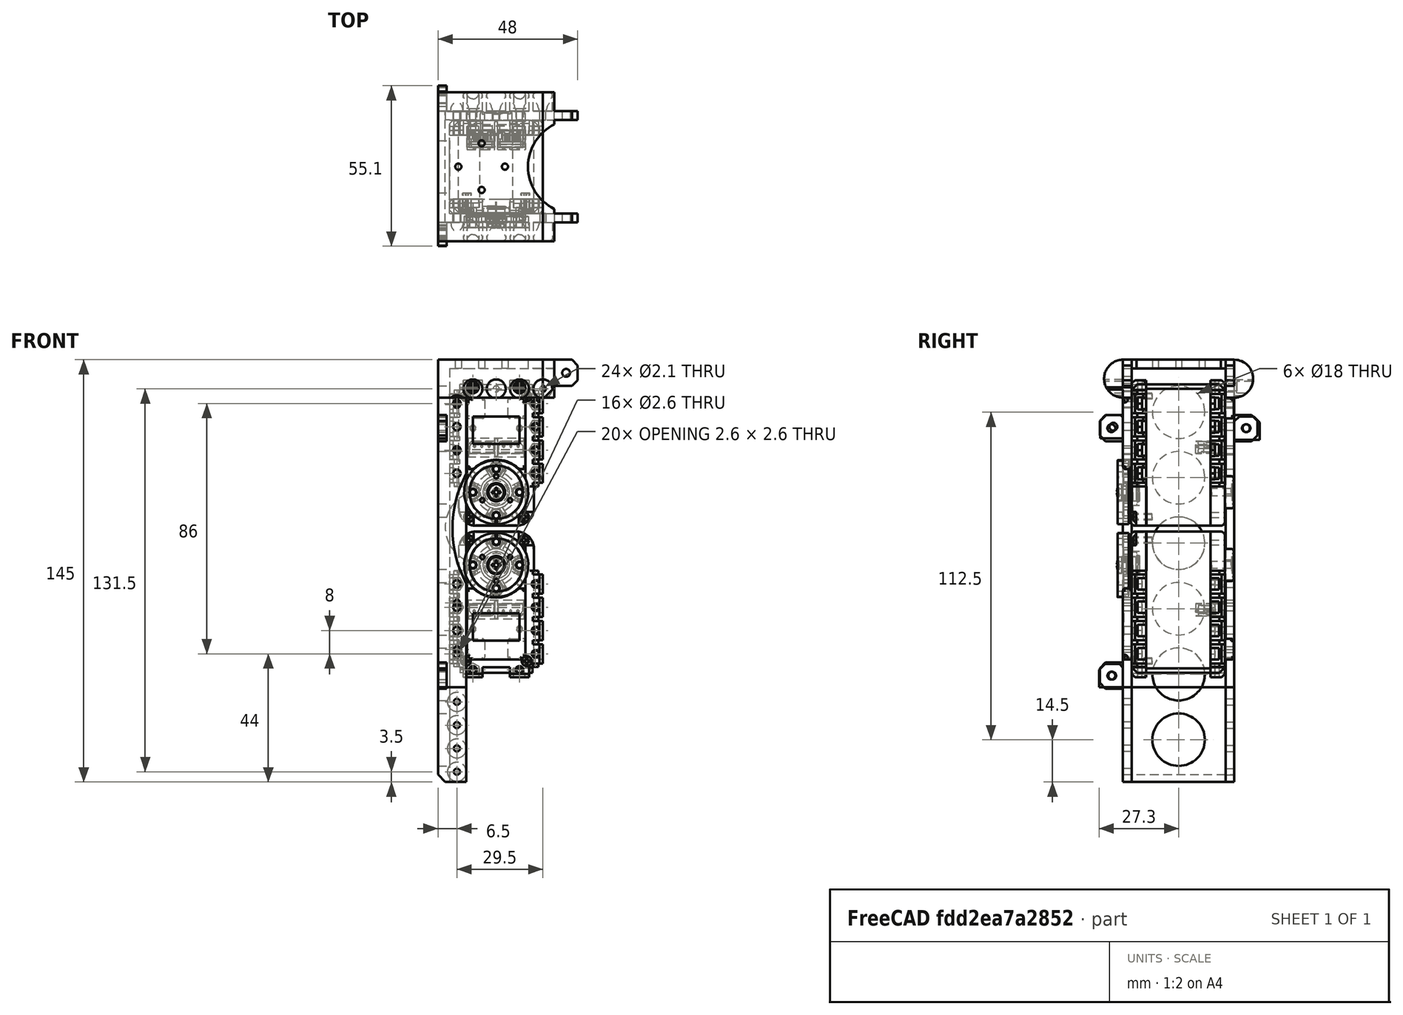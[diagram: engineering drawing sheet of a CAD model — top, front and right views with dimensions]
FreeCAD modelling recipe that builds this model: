
FCSTD DOCUMENT  (FreeCAD 0.16R6706 (Git))
Label: elbow_roll_frame_4_servo
License: CC-BY 3.0
LicenseURL: http://creativecommons.org/licenses/by/3.0/
objects: Part::Cylinder×76, Part::MultiFuse×40, Part::Box×22, Part::Cut×18, Part::Chamfer×7, Part::Mirroring×6, Part::Feature×2
note: 171 computed .brp shape members not serialized (recipe doc carries the construction recipe); baked Part::Feature solids carry a one-line shape summary decoded from their .brp

FEATURE [Part::Box] Box012  label="Cube012"
  Height = 3
  Length = 36
  Width = 38.2
FEATURE [Part::Box] Box013  label="Cube013"
  Height = 10
  Length = 36
  Placement = pos=(0,0,3) rot=(0,0,1;0rad)
  Width = 3
FEATURE [Part::Box] Box014  label="Cube014"
  Height = 10
  Length = 36
  Placement = pos=(0,35.2,3) rot=(0,0,1;0rad)
  Width = 3
FEATURE [Part::Cylinder] Cylinder068
  Angle = 360
  Height = 40
  Placement = pos=(-4,0,6.5) rot=(0,1,0;1.5708rad)
  Radius = 6.5
FEATURE [Part::Box] Box015  label="Cube015"
  Height = 20
  Length = 50
  Placement = pos=(-10,0,-5) rot=(0,0,1;0rad)
  Width = 10
FEATURE [Part::Cut] Cut008
  Base = -> Cylinder068
  Tool = -> Box015
FEATURE [Part::Box] Box016  label="Cube016"
  Height = 20
  Length = 50
  Placement = pos=(-10,0,-5) rot=(0,0,1;0rad)
  Width = 10
FEATURE [Part::Cylinder] Cylinder069
  Angle = 360
  Height = 40
  Placement = pos=(0,0,6.5) rot=(0,1,0;1.5708rad)
  Radius = 6.5
FEATURE [Part::Cut] Cut009
  Base = -> Cylinder069
  Placement = pos=(36,38.2,0) rot=(0,0,1;3.14159rad)
  Tool = -> Box016
FEATURE [Part::MultiFuse] Fusion041
  Shapes = -> [Box012,Box014,Box013,Cut008,Cut009]
FEATURE [Part::Cylinder] Cylinder070
  Angle = 360
  Height = 15
  Placement = pos=(16,4,10) rot=(1,0,0;1.5708rad)
  Radius = 1.05
FEATURE [Part::Cylinder] Cylinder071
  Angle = 360
  Height = 15
  Placement = pos=(24,4,10) rot=(1,0,0;1.5708rad)
  Radius = 1.05
FEATURE [Part::Cylinder] Cylinder072
  Angle = 360
  Height = 15
  Placement = pos=(32,4,10) rot=(1,0,0;1.5708rad)
  Radius = 1.05
FEATURE [Part::Cylinder] Cylinder073
  Angle = 360
  Height = 10
  Placement = pos=(8,0,10) rot=(1,0,0;1.5708rad)
  Radius = 3.25
FEATURE [Part::Cylinder] Cylinder074
  Angle = 360
  Height = 10
  Placement = pos=(8,0,10) rot=(1,0,0;1.5708rad)
  Radius = 3.25
FEATURE [Part::Cylinder] Cylinder075
  Angle = 360
  Height = 10
  Placement = pos=(16,0,10) rot=(1,0,0;1.5708rad)
  Radius = 3.25
FEATURE [Part::Cylinder] Cylinder076
  Angle = 360
  Height = 15
  Placement = pos=(8,4,10) rot=(1,0,0;1.5708rad)
  Radius = 1.05
FEATURE [Part::Cylinder] Cylinder077
  Angle = 360
  Height = 10
  Placement = pos=(24,0,10) rot=(1,0,0;1.5708rad)
  Radius = 3.25
FEATURE [Part::Cylinder] Cylinder078
  Angle = 360
  Height = 10
  Placement = pos=(32,0,10) rot=(1,0,0;1.5708rad)
  Radius = 3.25
FEATURE [Part::MultiFuse] Fusion042
  Shapes = -> [Cylinder070,Cylinder075,Cylinder074,Cylinder072,Cylinder078,Cylinder073,Cylinder077,Cylinder076,Cylinder071]
FEATURE [Part::Cylinder] Cylinder079
  Angle = 360
  Height = 15
  Placement = pos=(24,4,10) rot=(1,0,0;1.5708rad)
  Radius = 1.05
FEATURE [Part::Cylinder] Cylinder080
  Angle = 360
  Height = 15
  Placement = pos=(8,4,10) rot=(1,0,0;1.5708rad)
  Radius = 1.05
FEATURE [Part::Cylinder] Cylinder081
  Angle = 360
  Height = 10
  Placement = pos=(24,0,10) rot=(1,0,0;1.5708rad)
  Radius = 3.25
FEATURE [Part::Cylinder] Cylinder082
  Angle = 360
  Height = 10
  Placement = pos=(8,0,10) rot=(1,0,0;1.5708rad)
  Radius = 3.25
FEATURE [Part::Cylinder] Cylinder083
  Angle = 360
  Height = 10
  Placement = pos=(32,0,10) rot=(1,0,0;1.5708rad)
  Radius = 3.25
FEATURE [Part::Cylinder] Cylinder084
  Angle = 360
  Height = 10
  Placement = pos=(8,0,10) rot=(1,0,0;1.5708rad)
  Radius = 3.25
FEATURE [Part::Cylinder] Cylinder085
  Angle = 360
  Height = 15
  Placement = pos=(32,4,10) rot=(1,0,0;1.5708rad)
  Radius = 1.05
FEATURE [Part::Cylinder] Cylinder086
  Angle = 360
  Height = 10
  Placement = pos=(16,0,10) rot=(1,0,0;1.5708rad)
  Radius = 3.25
FEATURE [Part::Cylinder] Cylinder087
  Angle = 360
  Height = 15
  Placement = pos=(16,4,10) rot=(1,0,0;1.5708rad)
  Radius = 1.05
FEATURE [Part::MultiFuse] Fusion043
  Placement = pos=(40,38.2,0) rot=(0,0,1;3.14159rad)
  Shapes = -> [Cylinder087,Cylinder086,Cylinder084,Cylinder085,Cylinder083,Cylinder082,Cylinder081,Cylinder080,Cylinder079]
FEATURE [Part::MultiFuse] Fusion044
  Shapes = -> [Fusion042,Fusion043]
FEATURE [Part::Cylinder] Cylinder088
  Angle = 360
  Height = 10
  Placement = pos=(3,19.1,-3) rot=(0,0,1;0rad)
  Radius = 1.05
FEATURE [Part::Cylinder] Cylinder089
  Angle = 360
  Height = 10
  Placement = pos=(19,19.1,-3) rot=(0,0,1;0rad)
  Radius = 1.05
FEATURE [Part::Cylinder] Cylinder090
  Angle = 360
  Height = 10
  Placement = pos=(11,11.1,-3) rot=(0,0,1;0rad)
  Radius = 1.05
FEATURE [Part::Cylinder] Cylinder091
  Angle = 360
  Height = 10
  Placement = pos=(11,27.1,-3) rot=(0,0,1;0rad)
  Radius = 1.05
FEATURE [Part::MultiFuse] Fusion045
  Shapes = -> [Cylinder088,Cylinder091,Cylinder089,Cylinder090]
FEATURE [Part::Cylinder] Cylinder092
  Angle = 360
  Height = 10
  Placement = pos=(43,19.1,-3) rot=(0,0,1;0rad)
  Radius = 16.1
FEATURE [Part::MultiFuse] Fusion046
  Shapes = -> [Fusion045,Fusion044]
FEATURE [Part::Box] Box017  label="Cube017"
  Height = 10
  Length = 10
  Placement = pos=(29.5,-10,16) rot=(0,1,0;0.785398rad)
  Width = 20
FEATURE [Part::Box] Box018  label="Cube018"
  Height = 145
  Length = 4
  Placement = pos=(-4,0,0) rot=(0,0,1;0rad)
  Width = 38.2
FEATURE [Part::Box] Box019  label="Cube019"
  Height = 145
  Length = 5.75
  Width = 3
FEATURE [Part::Box] Box020  label="Cube020"
  Height = 145
  Length = 5.75
  Placement = pos=(0,35.2,0) rot=(0,0,1;0rad)
  Width = 3
FEATURE [Part::Cylinder] Cylinder093
  Angle = 360
  Height = 3
  Placement = pos=(11,38.2,57.5) rot=(1,0,0;1.5708rad)
  Radius = 12.5
FEATURE [Part::MultiFuse] Fusion047
  Shapes = -> [Cylinder093,Box017,Cylinder092]
FEATURE [Part::MultiFuse] Fusion048
  Shapes = -> [Fusion041,Box018,Box019,Box020]
FEATURE [Part::Cylinder] Cylinder094
  Angle = 360
  Height = 15
  Placement = pos=(2.5,4,15.5) rot=(1,0,0;1.5708rad)
  Radius = 1.05
FEATURE [Part::Cylinder] Cylinder095
  Angle = 360
  Height = 10
  Placement = pos=(2.5,0,15.5) rot=(1,0,0;1.5708rad)
  Radius = 3.25
FEATURE [Part::MultiFuse] Fusion049
  Shapes = -> [Cylinder094,Cylinder095]
FEATURE [Part::Cylinder] Cylinder096
  Angle = 360
  Height = 10
  Placement = pos=(2.5,0,15.5) rot=(1,0,0;1.5708rad)
  Radius = 3.25
FEATURE [Part::Cylinder] Cylinder097
  Angle = 360
  Height = 15
  Placement = pos=(2.5,4,15.5) rot=(1,0,0;1.5708rad)
  Radius = 1.05
FEATURE [Part::MultiFuse] Fusion050
  Placement = pos=(0,0,16) rot=(0,0,1;0rad)
  Shapes = -> [Cylinder097,Cylinder096]
FEATURE [Part::Cylinder] Cylinder098
  Angle = 360
  Height = 10
  Placement = pos=(2.5,0,15.5) rot=(1,0,0;1.5708rad)
  Radius = 3.25
FEATURE [Part::Cylinder] Cylinder099
  Angle = 360
  Height = 15
  Placement = pos=(2.5,4,15.5) rot=(1,0,0;1.5708rad)
  Radius = 1.05
FEATURE [Part::MultiFuse] Fusion051
  Placement = pos=(0,0,68) rot=(0,0,1;0rad)
  Shapes = -> [Cylinder099,Cylinder098]
FEATURE [Part::Cylinder] Cylinder100
  Angle = 360
  Height = 10
  Placement = pos=(2.5,0,15.5) rot=(1,0,0;1.5708rad)
  Radius = 3.25
FEATURE [Part::Cylinder] Cylinder101
  Angle = 360
  Height = 15
  Placement = pos=(2.5,4,15.5) rot=(1,0,0;1.5708rad)
  Radius = 1.05
FEATURE [Part::MultiFuse] Fusion052
  Placement = pos=(0,0,84) rot=(0,0,1;0rad)
  Shapes = -> [Cylinder101,Cylinder100]
FEATURE [Part::MultiFuse] Fusion053
  Shapes = -> [Fusion052,Fusion051,Fusion050,Fusion049]
FEATURE [Part::MultiFuse] Fusion055
  Shapes = -> [Cylinder094,Cylinder095]
FEATURE [Part::MultiFuse] Fusion056
  Placement = pos=(0,0,16) rot=(0,0,1;0rad)
  Shapes = -> [Cylinder097,Cylinder096]
FEATURE [Part::MultiFuse] Fusion057
  Placement = pos=(0,0,68) rot=(0,0,1;0rad)
  Shapes = -> [Cylinder099,Cylinder098]
FEATURE [Part::MultiFuse] Fusion058
  Placement = pos=(0,0,84) rot=(0,0,1;0rad)
  Shapes = -> [Cylinder101,Cylinder100]
FEATURE [Part::MultiFuse] Fusion054
  Placement = pos=(5,38.2,0) rot=(0,0,1;3.14159rad)
  Shapes = -> [Fusion058,Fusion057,Fusion056,Fusion055]
FEATURE [Part::Cut] Cut010
  Base = -> Fusion048
  Tool = -> Fusion047
FEATURE [Part::Cylinder] Cylinder102 .. Cylinder105  x4 (patterned run collapsed; names and placements below)
  Angle = 360
  Height = 10
  Radius = 9
  placements: 4 in arithmetic series — first pos=(-5,19.1,20) rot=(0,1,0;1.5708rad), step (0,0,22.5), last pos=(-5,19.1,87.5) rot=(0,1,0;1.5708rad)
FEATURE [Part::Cylinder] Cylinder106
  Angle = 360
  Height = 10
  Placement = pos=(2.5,0,15.5) rot=(1,0,0;1.5708rad)
  Radius = 3.25
FEATURE [Part::Cylinder] Cylinder107
  Angle = 360
  Height = 15
  Placement = pos=(2.5,4,15.5) rot=(1,0,0;1.5708rad)
  Radius = 1.05
FEATURE [Part::MultiFuse] Fusion059
  Placement = pos=(0,0,102) rot=(0,0,1;0rad)
  Shapes = -> [Cylinder107,Cylinder106]
FEATURE [Part::Cylinder] Cylinder108
  Angle = 360
  Height = 10
  Placement = pos=(2.5,0,15.5) rot=(1,0,0;1.5708rad)
  Radius = 3.25
FEATURE [Part::Cylinder] Cylinder109
  Angle = 360
  Height = 15
  Placement = pos=(2.5,4,15.5) rot=(1,0,0;1.5708rad)
  Radius = 1.05
FEATURE [Part::MultiFuse] Fusion060
  Placement = pos=(0,0,110) rot=(0,0,1;0rad)
  Shapes = -> [Cylinder109,Cylinder108]
FEATURE [Part::Cylinder] Cylinder110
  Angle = 360
  Height = 10
  Placement = pos=(2.5,0,15.5) rot=(1,0,0;1.5708rad)
  Radius = 3.25
FEATURE [Part::Cylinder] Cylinder111
  Angle = 360
  Height = 15
  Placement = pos=(2.5,4,15.5) rot=(1,0,0;1.5708rad)
  Radius = 1.05
FEATURE [Part::MultiFuse] Fusion061
  Placement = pos=(0,0,118) rot=(0,0,1;0rad)
  Shapes = -> [Cylinder111,Cylinder110]
FEATURE [Part::Cylinder] Cylinder112
  Angle = 360
  Height = 10
  Placement = pos=(2.5,0,15.5) rot=(1,0,0;1.5708rad)
  Radius = 3.25
FEATURE [Part::Cylinder] Cylinder113
  Angle = 360
  Height = 15
  Placement = pos=(2.5,4,15.5) rot=(1,0,0;1.5708rad)
  Radius = 1.05
FEATURE [Part::MultiFuse] Fusion062
  Placement = pos=(0,0,126) rot=(0,0,1;0rad)
  Shapes = -> [Cylinder113,Cylinder112]
FEATURE [Part::MultiFuse] Fusion063
  Shapes = -> [Fusion062,Fusion061,Fusion060,Fusion059]
FEATURE [Part::Cylinder] Cylinder114
  Angle = 360
  Height = 10
  Placement = pos=(2.5,0,15.5) rot=(1,0,0;1.5708rad)
  Radius = 3.25
FEATURE [Part::Cylinder] Cylinder115
  Angle = 360
  Height = 15
  Placement = pos=(2.5,4,15.5) rot=(1,0,0;1.5708rad)
  Radius = 1.05
FEATURE [Part::MultiFuse] Fusion064
  Placement = pos=(0,0,102) rot=(0,0,1;0rad)
  Shapes = -> [Cylinder115,Cylinder114]
FEATURE [Part::Cylinder] Cylinder116
  Angle = 360
  Height = 10
  Placement = pos=(2.5,0,15.5) rot=(1,0,0;1.5708rad)
  Radius = 3.25
FEATURE [Part::Cylinder] Cylinder117
  Angle = 360
  Height = 15
  Placement = pos=(2.5,4,15.5) rot=(1,0,0;1.5708rad)
  Radius = 1.05
FEATURE [Part::MultiFuse] Fusion065
  Placement = pos=(0,0,110) rot=(0,0,1;0rad)
  Shapes = -> [Cylinder117,Cylinder116]
FEATURE [Part::Cylinder] Cylinder118
  Angle = 360
  Height = 10
  Placement = pos=(2.5,0,15.5) rot=(1,0,0;1.5708rad)
  Radius = 3.25
FEATURE [Part::Cylinder] Cylinder119
  Angle = 360
  Height = 15
  Placement = pos=(2.5,4,15.5) rot=(1,0,0;1.5708rad)
  Radius = 1.05
FEATURE [Part::MultiFuse] Fusion066
  Placement = pos=(0,0,118) rot=(0,0,1;0rad)
  Shapes = -> [Cylinder119,Cylinder118]
FEATURE [Part::Cylinder] Cylinder120
  Angle = 360
  Height = 10
  Placement = pos=(2.5,0,15.5) rot=(1,0,0;1.5708rad)
  Radius = 3.25
FEATURE [Part::Cylinder] Cylinder121
  Angle = 360
  Height = 15
  Placement = pos=(2.5,4,15.5) rot=(1,0,0;1.5708rad)
  Radius = 1.05
FEATURE [Part::MultiFuse] Fusion067
  Placement = pos=(0,0,126) rot=(0,0,1;0rad)
  Shapes = -> [Cylinder121,Cylinder120]
FEATURE [Part::MultiFuse] Fusion068
  Placement = pos=(5,38,0) rot=(0,0,1;3.14159rad)
  Shapes = -> [Fusion067,Fusion066,Fusion065,Fusion064]
FEATURE [Part::Cylinder] Cylinder122
  Angle = 360
  Height = 10
  Placement = pos=(-5,19.1,110) rot=(0,1,0;1.5708rad)
  Radius = 9
FEATURE [Part::Cylinder] Cylinder123
  Angle = 360
  Height = 10
  Placement = pos=(-5,19.1,132.5) rot=(0,1,0;1.5708rad)
  Radius = 9
FEATURE [Part::MultiFuse] Fusion069
  Placement = pos=(0,0,-2) rot=(0,0,1;0rad)
  Shapes = -> [Cylinder122,Cylinder105,Cylinder104,Cylinder102,Cylinder123,Cylinder103]
FEATURE [Part::MultiFuse] Fusion070
  Shapes = -> [Fusion069,Fusion068,Fusion063,Fusion046,Fusion053,Fusion054]
FEATURE [Part::Chamfer] Chamfer004
  Base = -> Cut010
  Edges = 1 edges r=2.5: [Edge5]
FEATURE [Part::Box] Box021  label="Cube021"
  Height = 8
  Length = 9
  Placement = pos=(-9,0,36) rot=(0,0,1;0rad)
  Width = 3
FEATURE [Part::Cylinder] Cylinder124
  Angle = 360
  Height = 10
  Placement = pos=(-4.5,5,40) rot=(1,0,0;1.5708rad)
  Radius = 1.35
FEATURE [Part::Cut] Cut012
  Base = -> Box021
  Tool = -> Cylinder124
FEATURE [Part::Chamfer] Chamfer005
  Base = -> Cut012
  Edges = 2 edges r=2: [Edge2,Edge10]
FEATURE [Part::Box] Box022  label="Cube022"
  Height = 8
  Length = 9
  Placement = pos=(-9,0,36) rot=(0,0,1;0rad)
  Width = 3
FEATURE [Part::Cylinder] Cylinder125
  Angle = 360
  Height = 10
  Placement = pos=(-4.5,5,40) rot=(1,0,0;1.5708rad)
  Radius = 1.35
FEATURE [Part::Cut] Cut013
  Base = -> Box022
  Tool = -> Cylinder125
FEATURE [Part::Chamfer] Chamfer006
  Base = -> Cut013
  Edges = 2 edges r=2: [Edge2,Edge10]
  Placement = pos=(0,35.2,0) rot=(0,0,1;0rad)
FEATURE [Part::MultiFuse] Fusion071
  Shapes = -> [Chamfer005,Chamfer006]
FEATURE [Part::Box] Box023  label="Cube023"
  Height = 8
  Length = 9
  Placement = pos=(-9,0,36) rot=(0,0,1;0rad)
  Width = 3
FEATURE [Part::Cylinder] Cylinder126
  Angle = 360
  Height = 10
  Placement = pos=(-4.5,5,40) rot=(1,0,0;1.5708rad)
  Radius = 1.35
FEATURE [Part::Cut] Cut014
  Base = -> Box023
  Tool = -> Cylinder126
FEATURE [Part::Chamfer] Chamfer007
  Base = -> Cut014
  Edges = 2 edges r=2: [Edge2,Edge10]
  Placement = pos=(-19,2.2,-1) rot=(-1,0,0;1.5708rad)
FEATURE [Part::Mirroring] Part__Mirroring003  label="Chamfer003 (Mirror #1)001"
  Base = (0,19.1,0)
  Normal = (0,1,0)
  Source = -> Chamfer007
FEATURE [Part::Mirroring] Part__Mirroring004  label="Chamfer003 (Mirror #2)001"
  Base = (-66,0,0)
  Normal = (1,0,0)
  Source = -> Part__Mirroring003
FEATURE [Part::Feature] Part__Feature062  label="servo"
  Placement = pos=(16,-8,-20.5) rot=(0,1,0;3.14159rad)
  shape: bbox 32 x 40.05 x 50.5 mm, 1149 faces (baked)
FEATURE [Part::Cut] Cut011
  Base = -> Chamfer004
  Placement = pos=(0,0,0) rot=(0,-1,0;1.5708rad)
  Tool = -> Fusion070
FEATURE [Part::MultiFuse] Fusion074  label="nut"
  Shapes = -> [Chamfer007,Part__Mirroring003,Part__Mirroring004,Fusion071]
FEATURE [Part::MultiFuse] Fusion075
  Shapes = -> [Cut011,Fusion074]
FEATURE [Part::Mirroring] Part__Mirroring  label="OLD"
  Base = (0,0,0)
  Normal = (0,0,1)
  Placement = pos=(0,0,0) rot=(0,-1,0;1.5708rad)
  Source = -> Fusion075
FEATURE [Part::Mirroring] Part__Mirroring006  label="servo001"
  Base = (16,20.0226,0)
  Normal = (0,0,1)
  Placement = pos=(0,27,-66) rot=(0,0,1;0rad)
  Source = -> Part__Feature062
FEATURE [Part::Feature] Part__Feature063  label="servo002"
  Placement = pos=(16,-8,-20.5) rot=(0,1,0;3.14159rad)
  shape: bbox 32 x 40.05 x 50.5 mm, 1149 faces (baked)
FEATURE [Part::Mirroring] Part__Mirroring007  label="servo003"
  Base = (16,19.9898,0)
  Normal = (0,0,1)
  Placement = pos=(32,27,-50) rot=(0,1,0;3.14159rad)
  Source = -> Part__Feature063
FEATURE [Part::MultiFuse] Fusion086  label="Servos"
  Placement = pos=(32,38,0) rot=(0,0,1;3.14159rad)
  Shapes = -> [Part__Mirroring006,Part__Mirroring007]
FEATURE [Part::Chamfer] Chamfer011
  Edges = 2 edges r=2: [Edge2,Edge10]
  Placement = pos=(-4,37.9,-63.5) rot=(0,0,-1;1.5708rad)
FEATURE [Part::Chamfer] Chamfer012
  Edges = 2 edges r=2: [Edge2,Edge10]
  Placement = pos=(-4,-8.2,-148.5) rot=(0,0,-1;1.5708rad)
FEATURE [Part::Chamfer] Chamfer013
  Edges = 2 edges r=2: [Edge2,Edge10]
  Placement = pos=(-4,-7.8,-63) rot=(0,0,-1;1.5708rad)
FEATURE [Part::Box] Box  label="Cubo"
  Height = 50
  Length = 50
  Placement = pos=(-4,-8,-162.5) rot=(0,0,1;0rad)
  Width = 50
FEATURE [Part::MultiFuse] Fusion091  label="nut hole "
  Shapes = -> [Chamfer013,Chamfer012,Chamfer011]
FEATURE [Part::Box] Box041  label="Cubo001"
  Height = 50
  Length = 10
  Placement = pos=(32,-16,-19) rot=(0,0,1;0rad)
  Width = 100
FEATURE [Part::Box] Box043  label="Cube041"
  Height = 3
  Length = 36
  Width = 38.2
FEATURE [Part::Box] Box044  label="Cube042"
  Height = 10
  Length = 36
  Placement = pos=(0,0,3) rot=(0,0,1;0rad)
  Width = 3
FEATURE [Part::Box] Box045  label="Cube043"
  Height = 10
  Length = 36
  Placement = pos=(0,35.2,3) rot=(0,0,1;0rad)
  Width = 3
FEATURE [Part::Cylinder] Cylinder164
  Angle = 360
  Height = 40
  Placement = pos=(-4,0,6.5) rot=(0,1,0;1.5708rad)
  Radius = 6.5
FEATURE [Part::Box] Box046  label="Cube044"
  Height = 20
  Length = 50
  Placement = pos=(-10,0,-5) rot=(0,0,1;0rad)
  Width = 10
FEATURE [Part::Cut] Cut034
  Base = -> Cylinder164
  Tool = -> Box046
FEATURE [Part::Box] Box047  label="Cube045"
  Height = 20
  Length = 50
  Placement = pos=(-10,0,-5) rot=(0,0,1;0rad)
  Width = 10
FEATURE [Part::Cylinder] Cylinder165
  Angle = 360
  Height = 40
  Placement = pos=(0,0,6.5) rot=(0,1,0;1.5708rad)
  Radius = 6.5
FEATURE [Part::Cut] Cut035
  Base = -> Cylinder165
  Placement = pos=(36,38.2,0) rot=(0,0,1;3.14159rad)
  Tool = -> Box047
FEATURE [Part::MultiFuse] Fusion092
  Shapes = -> [Box043,Box045,Box044,Cut034,Cut035]
FEATURE [Part::Box] Box048  label="Cube046"
  Height = 145
  Length = 4
  Placement = pos=(-4,0,0) rot=(0,0,1;0rad)
  Width = 38.2
FEATURE [Part::Box] Box049  label="Cube047"
  Height = 145
  Length = 5.75
  Width = 3
FEATURE [Part::Box] Box050  label="Cube048"
  Height = 145
  Length = 5.75
  Placement = pos=(0,35.2,0) rot=(0,0,1;0rad)
  Width = 3
FEATURE [Part::MultiFuse] Fusion093
  Shapes = -> [Fusion092,Box048,Box049,Box050]
FEATURE [Part::Mirroring] Part__Mirroring009  label="Fusion083 (Mirror #4)002"
  Base = (0,0,0)
  Normal = (0,0,1)
  Source = -> Fusion093
FEATURE [Part::Cylinder] Cylinder166  label="Cilindro034"
  Angle = 360
  Height = 60
  Placement = pos=(8,48,-9.5) rot=(1,0,0;1.5708rad)
  Radius = 1.3
FEATURE [Part::Cylinder] Cylinder167  label="Cilindro035"
  Angle = 360
  Height = 60
  Placement = pos=(24,48,-9.5) rot=(1,0,0;1.5708rad)
  Radius = 1.3
FEATURE [Part::Cylinder] Cylinder168  label="Cilindro036"
  Angle = 360
  Height = 60
  Placement = pos=(2.5,48,-15) rot=(1,0,0;1.5708rad)
  Radius = 1.3
FEATURE [Part::Cylinder] Cylinder169  label="Cilindro037"
  Angle = 360
  Height = 60
  Placement = pos=(2.5,48,-23) rot=(1,0,0;1.5708rad)
  Radius = 1.3
FEATURE [Part::Cylinder] Cylinder170  label="Cilindro038"
  Angle = 360
  Height = 60
  Placement = pos=(2.5,48,-31) rot=(1,0,0;1.5708rad)
  Radius = 1.3
FEATURE [Part::Cylinder] Cylinder171  label="Cilindro039"
  Angle = 360
  Height = 60
  Placement = pos=(2.5,48,-39) rot=(1,0,0;1.5708rad)
  Radius = 1.3
FEATURE [Part::MultiFuse] Fusion094
  Shapes = -> [Cylinder171,Cylinder170,Cylinder169,Cylinder168,Cylinder167,Cylinder166]
FEATURE [Part::Cut] Cut036
  Base = -> Part__Mirroring009
  Tool = -> Fusion094
FEATURE [Part::Cylinder] Cylinder172  label="Cilindro040"
  Angle = 360
  Height = 60
  Placement = pos=(2.5,48,-15) rot=(1,0,0;1.5708rad)
  Radius = 1.3
FEATURE [Part::Cylinder] Cylinder173  label="Cilindro041"
  Angle = 360
  Height = 60
  Placement = pos=(2.5,48,-23) rot=(1,0,0;1.5708rad)
  Radius = 1.3
FEATURE [Part::Cylinder] Cylinder174  label="Cilindro042"
  Angle = 360
  Height = 60
  Placement = pos=(2.5,48,-39) rot=(1,0,0;1.5708rad)
  Radius = 1.3
FEATURE [Part::Cylinder] Cylinder175  label="Cilindro043"
  Angle = 360
  Height = 60
  Placement = pos=(2.5,48,-31) rot=(1,0,0;1.5708rad)
  Radius = 1.3
FEATURE [Part::MultiFuse] Fusion095  label="hole004"
  Placement = pos=(0,0,-62) rot=(0,0,1;0rad)
  Shapes = -> [Cylinder172,Cylinder173,Cylinder174,Cylinder175]
FEATURE [Part::Cut] Cut037
  Base = -> Cut036
  Tool = -> Fusion095
FEATURE [Part::Cylinder] Cylinder176  label="Cilindro044"
  Angle = 276
  Height = 20
  Placement = pos=(41,15,-58) rot=(1,0,0;1.5708rad)
  Radius = 40
FEATURE [Part::Cut] Cut038  label="buono "
  Base = -> Cut037
  Tool = -> Cylinder176
FEATURE [Part::Cylinder] Cylinder177  label="Cilindro045"
  Angle = 360
  Height = 10
  Placement = pos=(8,0,-9.5) rot=(1,0,0;1.5708rad)
  Radius = 2
FEATURE [Part::Cylinder] Cylinder178  label="Cilindro046"
  Angle = 360
  Height = 10
  Placement = pos=(8,49,-9.5) rot=(1,0,0;1.5708rad)
  Radius = 2
FEATURE [Part::Cylinder] Cylinder179  label="Cilindro047"
  Angle = 360
  Height = 10
  Placement = pos=(24,0,-9.5) rot=(1,0,0;1.5708rad)
  Radius = 2
FEATURE [Part::Cylinder] Cylinder180  label="Cilindro048"
  Angle = 360
  Height = 10
  Placement = pos=(24,49,-9.5) rot=(1,0,0;1.5708rad)
  Radius = 2
FEATURE [Part::Cut] Cut039
  Base = -> Cut038
  Tool = -> Box041
FEATURE [Part::Cut] Cut040
  Base = -> Cut039
  Tool = -> Cylinder180
FEATURE [Part::Cut] Cut041
  Base = -> Cut040
  Tool = -> Cylinder179
FEATURE [Part::Cut] Cut042
  Base = -> Cut041
  Tool = -> Cylinder178
FEATURE [Part::Cut] Cut043
  Base = -> Cut042
  Tool = -> Cylinder177
FEATURE [Part::Cut] Cut044  label="good"
  Base = -> Cut043
  Tool = -> Box
FEATURE [Part::MultiFuse] Fusion096  label="Arm"
  Shapes = -> [Cut044,Fusion091]
